# Revit family: Barreira 1000 Shower Screen
name_source: partatom
category: Plumbing Fixtures
units: mm (PartAtom-declared; Revit-internal decimal feet)

## family parameters
Always vertical = Yes
Cut with Voids When Loaded = No
Enable Cutting in Views = No
Maintain Annotation Orientation = No
OmniClass Number = 23.45.00.00
OmniClass Title = Sanitary, Laundry, and Cleaning Equipment
Part Type = Normal
Room Calculation Point = No
Round Connector Dimension = Use Diameter
Shared = No
Work Plane-Based = No

## types (2) — shared parameters
Category = Shower Screens
Fixing Details = Stainlesss Steel Stabiliser Bar (Adjustable)
Glass = Glass
Manufacturer = Lecico SA
Material = Toughened Safety Glass
Technical Dimensions = W1000 x H2000 x D06mm
URL = https://www.lecicosa.co.za
zero-valued in all types: Default Elevation

## per-type parameters (varying)
| type | Colour | Model | Product Code | Stainless Steel |
| Barriere 1000 Shower Screen - Silver | Silver | Barriere 1000 Shower Screen -Silver | SHOSCRBARSILVBS | Stainless Steel, Polished |
| Barriere 1000 Shower Screen - Black | Black | Barriere 1000 Shower Screen -Black | SHOSCRBARBLACBS | Black Powdercoat |

## geometry (parser evidence)
native form markers: Sweep x2
no freeform markers — native parametric forms only
